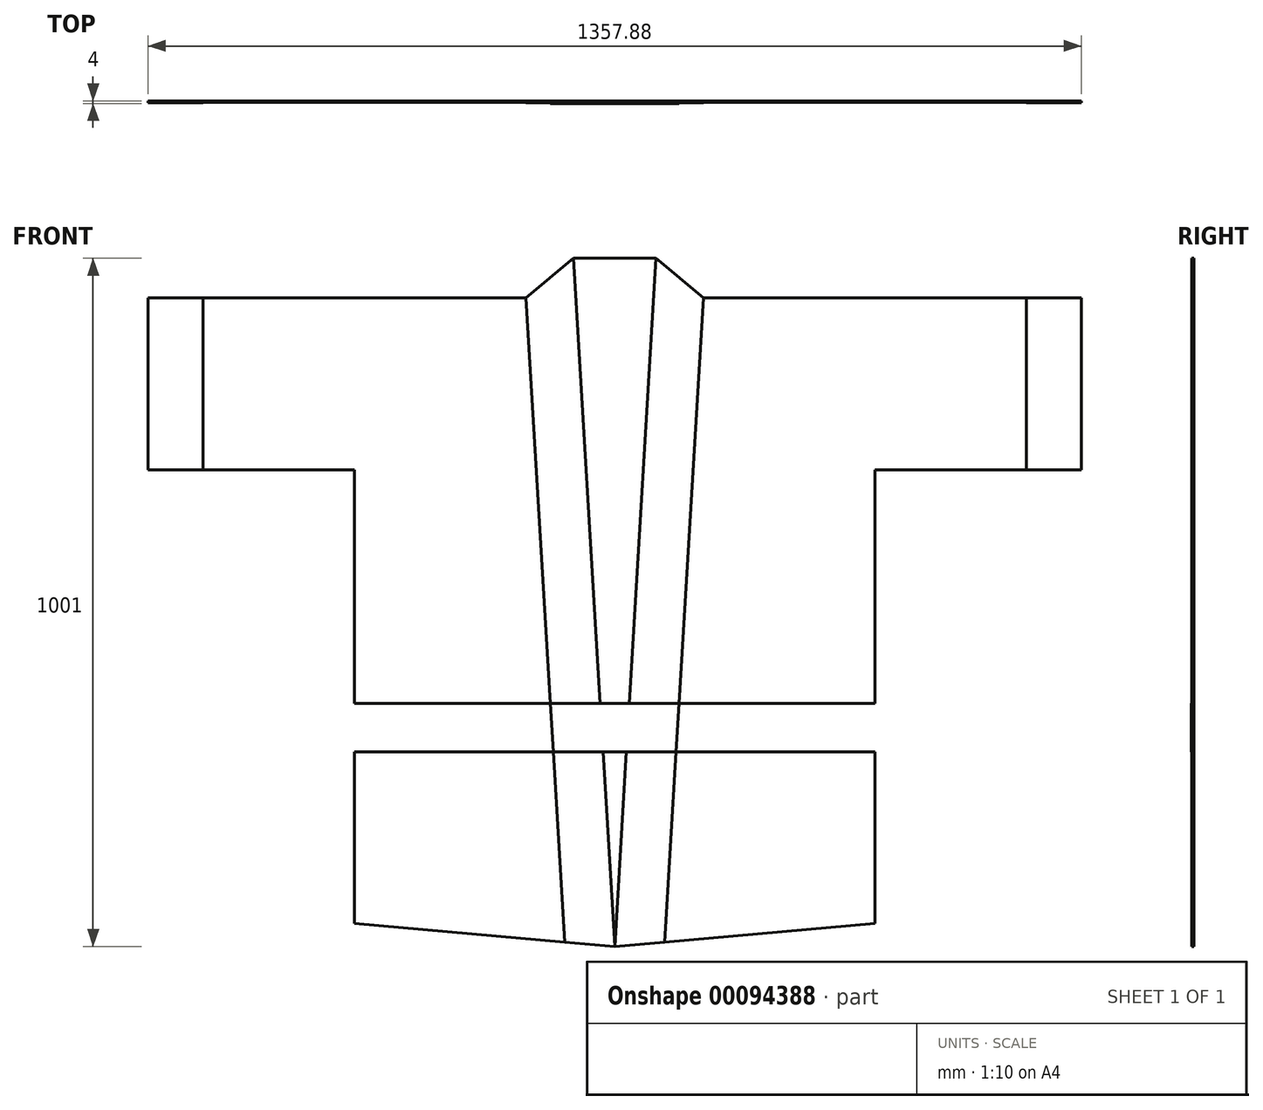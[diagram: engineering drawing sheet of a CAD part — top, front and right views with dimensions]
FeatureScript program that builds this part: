
annotation { "Feature Type Name" : "Feature", "Feature Type Description" : "" }
export const myFeature = defineFeature(function(context is Context, id is Id, definition is map)
    precondition{}
    {
        {
            var Q0;
            Q0=qCreatedBy(makeId("Front.planeOp"),FACE);
            var sketch = newSketch(context, id + "F0", { "sketchPlane" : qUnion([Q0])});
            skLineSegment(sketch, "E0", {"start": v(-378.94, 0) * mm, "end": v(-678.94, 0) * mm});
            skLineSegment(sketch, "E1", {"start": v(-678.94, 0) * mm, "end": v(-678.94, 250) * mm});
            skLineSegment(sketch, "E2", {"start": v(-678.94, 250) * mm, "end": v(-128.94, 250) * mm});
            skLineSegment(sketch, "E3", {"start": v(-128.94, 250) * mm, "end": v(-60, 307.85) * mm});
            skLineSegment(sketch, "E4", {"start": v(-60, 307.85) * mm, "end": v(0, 307.85) * mm});
            skLineSegment(sketch, "E5", {"start": v(-378.94, 0) * mm, "end": v(-378.94, -660) * mm});
            skLineSegment(sketch, "E6", {"start": v(-378.94, -660) * mm, "end": v(0, -693.15) * mm});
            skLineSegment(sketch, "E7", {"start": v(0, 307.85) * mm, "end": v(0, -693.15) * mm, "construction": true});
            skLineSegment(sketch, "E8", {"start": v(-60, 307.85) * mm, "end": v(0, -693.15) * mm});
            skLineSegment(sketch, "E9", {"start": v(-128.94, 250) * mm, "end": v(-72.8, -686.78) * mm});
            skLineSegment(sketch, "E10.MirrorCS", {"start": v(378.94, 0) * mm, "end": v(678.94, 0) * mm});
            skLineSegment(sketch, "E11.MirrorCS", {"start": v(678.94, 0) * mm, "end": v(678.94, 250) * mm});
            skLineSegment(sketch, "E12.MirrorCS", {"start": v(128.94, 250) * mm, "end": v(60, 307.85) * mm});
            skLineSegment(sketch, "E13.MirrorCS", {"start": v(128.94, 250) * mm, "end": v(72.8, -686.78) * mm});
            skLineSegment(sketch, "E14.MirrorCS", {"start": v(378.94, 0) * mm, "end": v(378.94, -660) * mm});
            skLineSegment(sketch, "E15.MirrorCS", {"start": v(678.94, 250) * mm, "end": v(128.94, 250) * mm});
            skLineSegment(sketch, "E16.MirrorCS", {"start": v(60, 307.85) * mm, "end": v(0, 307.85) * mm});
            skLineSegment(sketch, "E17.MirrorCS", {"start": v(378.94, -660) * mm, "end": v(0, -693.15) * mm});
            skLineSegment(sketch, "E18.MirrorCS", {"start": v(60, 307.85) * mm, "end": v(0, -693.15) * mm});
            skLineSegment(sketch, "E19", {"start": v(-678.94, 0) * mm, "end": v(-598.94, 0) * mm, "construction": true});
            skLineSegment(sketch, "E20", {"start": v(-598.94, 0) * mm, "end": v(-598.94, 250) * mm});
            skLineSegment(sketch, "E21.MirrorCS", {"start": v(598.94, 0) * mm, "end": v(598.94, 250) * mm});
            skLineSegment(sketch, "E22.bottom", {"start": v(-378.94, -340) * mm, "end": v(378.94, -340) * mm});
            skLineSegment(sketch, "E22.top", {"start": v(-378.94, -410) * mm, "end": v(378.94, -410) * mm});
            skLineSegment(sketch, "E22.left", {"start": v(-378.94, -340) * mm, "end": v(-378.94, -410) * mm});
            skLineSegment(sketch, "E22.right", {"start": v(378.94, -340) * mm, "end": v(378.94, -410) * mm});
            skLineSegment(sketch, "E23", {"start": v(378.94, -660) * mm, "end": v(378.94, -410) * mm, "construction": true});
            skSolve(sketch);
        }
        {
            var Q0;
            {var subQ4=sQuery(id+"F0.wireOp",EDGE,"E4");Q0=makeQuery(id+"F0.imprint","IMPRINT",FACE,{"disambiguationData":[TD([[makeQuery(id+"F0.imprint","IMPRINT",EDGE,{"derivedFrom":subQ4}),-1.0]])]});}
            var Q1;
            {var subQ1=sQuery(id+"F0.wireOp",EDGE,"E8");var subQ3=sQuery(id+"F0.wireOp",EDGE,"E22.top");var subQ4=makeQuery(id+"F0.imprint","INTERSECT",VERTEX,{"derivedFrom":[subQ1,subQ3]});Q1=makeQuery(id+"F0.imprint","IMPRINT",FACE,{"disambiguationData":[TD([[makeQuery(id+"F0.imprint","IMPRINT",EDGE,{"disambiguationData":[TD([[subQ4,-1.0]])],"derivedFrom":subQ3}),-1.0]])]});}
            extrude(context, id + "F1", {"entities" : qUnion([Q0, Q1]), "depth" : 1 * mm});
        }
        {
            var Q0;
            {var subQ3=sQuery(id+"F0.wireOp",EDGE,"E21.MirrorCS");Q0=makeQuery(id+"F0.imprint","IMPRINT",FACE,{"disambiguationData":[TD([[makeQuery(id+"F0.imprint","IMPRINT",EDGE,{"derivedFrom":subQ3}),1.0]])]});}
            var Q1;
            {var subQ9=sQuery(id+"F0.wireOp",EDGE,"E20");Q1=makeQuery(id+"F0.imprint","IMPRINT",FACE,{"disambiguationData":[TD([[makeQuery(id+"F0.imprint","IMPRINT",EDGE,{"derivedFrom":subQ9}),-1.0]])]});}
            var Q2;
            {var subQ0=sQuery(id+"F0.wireOp",EDGE,"E6");var subQ1=sQuery(id+"F0.wireOp",EDGE,"E5");var subQ2=makeQuery(id+"F0.imprint","INTERSECT",VERTEX,{"derivedFrom":[subQ1,subQ0]});Q2=makeQuery(id+"F0.imprint","IMPRINT",FACE,{"disambiguationData":[TD([[makeQuery(id+"F0.imprint","IMPRINT",EDGE,{"disambiguationData":[TD([[subQ2,-1.0]])],"derivedFrom":subQ0}),1.0]])]});}
            var Q3;
            {var subQ0=sQuery(id+"F0.wireOp",EDGE,"E17.MirrorCS");var subQ1=sQuery(id+"F0.wireOp",EDGE,"E13.MirrorCS");var subQ2=makeQuery(id+"F0.imprint","INTERSECT",VERTEX,{"derivedFrom":[subQ1,subQ0]});Q3=makeQuery(id+"F0.imprint","IMPRINT",FACE,{"disambiguationData":[TD([[makeQuery(id+"F0.imprint","IMPRINT",EDGE,{"disambiguationData":[TD([[subQ2,1.0]])],"derivedFrom":subQ1}),1.0]])]});}
            extrude(context, id + "F2", {"entities" : qUnion([Q0, Q1, Q2, Q3]), "depth" : 2 * mm});
        }
        {
            var Q0;
            {var subQ0=sQuery(id+"F0.wireOp",EDGE,"E11.MirrorCS");Q0=makeQuery(id+"F0.imprint","IMPRINT",FACE,{"disambiguationData":[TD([[makeQuery(id+"F0.imprint","IMPRINT",EDGE,{"derivedFrom":subQ0}),1.0]])]});}
            var Q1;
            {var subQ0=sQuery(id+"F0.wireOp",EDGE,"E12.MirrorCS");Q1=makeQuery(id+"F0.imprint","IMPRINT",FACE,{"disambiguationData":[TD([[makeQuery(id+"F0.imprint","IMPRINT",EDGE,{"derivedFrom":subQ0}),1.0]])]});}
            var Q2;
            {var subQ0=sQuery(id+"F0.wireOp",EDGE,"E3");Q2=makeQuery(id+"F0.imprint","IMPRINT",FACE,{"disambiguationData":[TD([[makeQuery(id+"F0.imprint","IMPRINT",EDGE,{"derivedFrom":subQ0}),-1.0]])]});}
            var Q3;
            {var subQ0=sQuery(id+"F0.wireOp",EDGE,"E1");Q3=makeQuery(id+"F0.imprint","IMPRINT",FACE,{"disambiguationData":[TD([[makeQuery(id+"F0.imprint","IMPRINT",EDGE,{"derivedFrom":subQ0}),-1.0]])]});}
            var Q4;
            {var subQ1=sQuery(id+"F0.wireOp",EDGE,"E6");var subQ3=sQuery(id+"F0.wireOp",EDGE,"E9");var subQ4=makeQuery(id+"F0.imprint","INTERSECT",VERTEX,{"derivedFrom":[subQ1,subQ3]});Q4=makeQuery(id+"F0.imprint","IMPRINT",FACE,{"disambiguationData":[TD([[makeQuery(id+"F0.imprint","IMPRINT",EDGE,{"disambiguationData":[TD([[subQ4,1.0]])],"derivedFrom":subQ3}),1.0]])]});}
            var Q5;
            {var subQ0=sQuery(id+"F0.wireOp",EDGE,"E17.MirrorCS");var subQ1=sQuery(id+"F0.wireOp",EDGE,"E13.MirrorCS");var subQ2=makeQuery(id+"F0.imprint","INTERSECT",VERTEX,{"derivedFrom":[subQ1,subQ0]});Q5=makeQuery(id+"F0.imprint","IMPRINT",FACE,{"disambiguationData":[TD([[makeQuery(id+"F0.imprint","IMPRINT",EDGE,{"disambiguationData":[TD([[subQ2,1.0]])],"derivedFrom":subQ1}),-1.0]])]});}
            extrude(context, id + "F3", {"entities" : qUnion([Q0, Q1, Q2, Q3, Q4, Q5]), "depth" : 3 * mm});
        }
        {
            var Q0;
            {var subQ5=sQuery(id+"F0.wireOp",EDGE,"E22.left");Q0=makeQuery(id+"F0.imprint","IMPRINT",FACE,{"disambiguationData":[TD([[makeQuery(id+"F0.imprint","IMPRINT",EDGE,{"derivedFrom":subQ5}),1.0]])]});}
            var Q1;
            {var subQ0=sQuery(id+"F0.wireOp",EDGE,"E22.bottom");var subQ1=sQuery(id+"F0.wireOp",EDGE,"E8");var subQ2=makeQuery(id+"F0.imprint","INTERSECT",VERTEX,{"derivedFrom":[subQ1,subQ0]});Q1=makeQuery(id+"F0.imprint","IMPRINT",FACE,{"disambiguationData":[TD([[makeQuery(id+"F0.imprint","IMPRINT",EDGE,{"disambiguationData":[TD([[subQ2,-1.0]])],"derivedFrom":subQ1}),-1.0]])]});}
            var Q2;
            {var subQ0=sQuery(id+"F0.wireOp",EDGE,"E22.bottom");var subQ1=sQuery(id+"F0.wireOp",EDGE,"E13.MirrorCS");var subQ2=makeQuery(id+"F0.imprint","INTERSECT",VERTEX,{"derivedFrom":[subQ1,subQ0]});Q2=makeQuery(id+"F0.imprint","IMPRINT",FACE,{"disambiguationData":[TD([[makeQuery(id+"F0.imprint","IMPRINT",EDGE,{"disambiguationData":[TD([[subQ2,-1.0]])],"derivedFrom":subQ1}),-1.0]])]});}
            var Q3;
            {var subQ5=sQuery(id+"F0.wireOp",EDGE,"E22.right");Q3=makeQuery(id+"F0.imprint","IMPRINT",FACE,{"disambiguationData":[TD([[makeQuery(id+"F0.imprint","IMPRINT",EDGE,{"derivedFrom":subQ5}),-1.0]])]});}
            var Q4;
            {var subQ0=sQuery(id+"F0.wireOp",EDGE,"E22.bottom");var subQ1=sQuery(id+"F0.wireOp",EDGE,"E8");var subQ2=makeQuery(id+"F0.imprint","INTERSECT",VERTEX,{"derivedFrom":[subQ1,subQ0]});Q4=makeQuery(id+"F0.imprint","IMPRINT",FACE,{"disambiguationData":[TD([[makeQuery(id+"F0.imprint","IMPRINT",EDGE,{"disambiguationData":[TD([[subQ2,-1.0]])],"derivedFrom":subQ1}),1.0]])]});}
            extrude(context, id + "F4", {"entities" : qUnion([Q0, Q1, Q2, Q3, Q4]), "depth" : 4 * mm});
        }
    });
